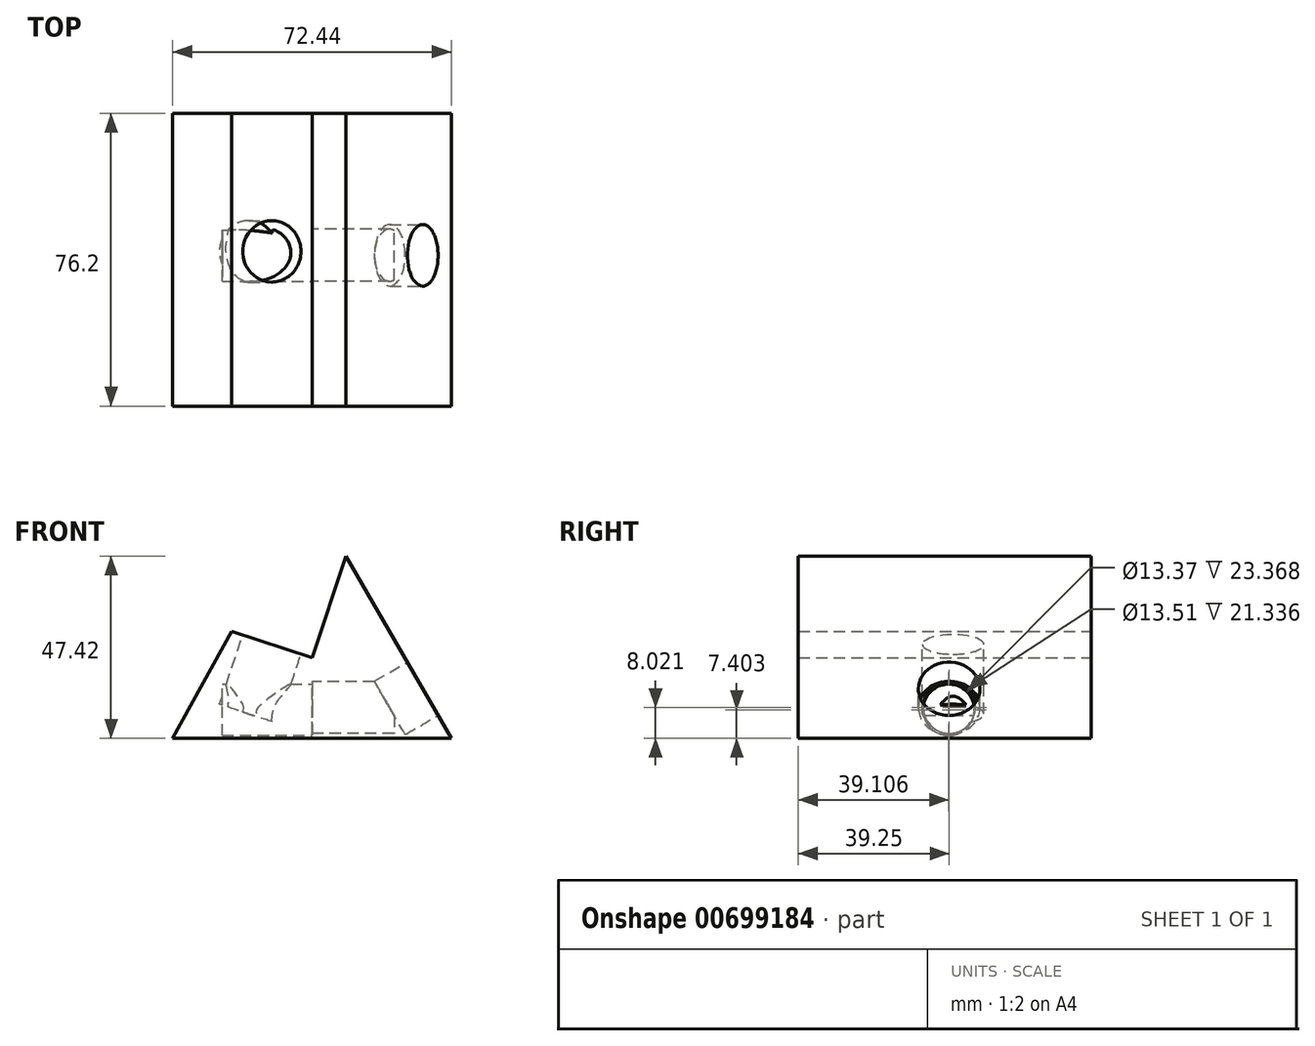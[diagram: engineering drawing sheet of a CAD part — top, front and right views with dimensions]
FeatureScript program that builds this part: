
annotation { "Feature Type Name" : "Feature", "Feature Type Description" : "" }
export const myFeature = defineFeature(function(context is Context, id is Id, definition is map)
    precondition{}
    {
        {
            var Q0;
            Q0=qCreatedBy(makeId("Front.planeOp"),FACE);
            var sketch = newSketch(context, id + "F0", { "sketchPlane" : qUnion([Q0])});
            skLineSegment(sketch, "E0.0", {"start": v(36.22, -20.9) * mm, "end": v(-36.22, -20.9) * mm});
            skLineSegment(sketch, "E0.1", {"start": v(-36.22, -20.9) * mm, "end": v(-20.9, 6.97) * mm});
            skLineSegment(sketch, "E0.2", {"start": v(8.84, 26.51) * mm, "end": v(36.22, -20.9) * mm});
            skPoint(sketch, "E0.0.midPoint", {"position": v(0, -20.9) * mm});
            skPoint(sketch, "E0.cCircle.center.orphan", {"position": v(0, 0) * mm});
            skLineSegment(sketch, "E1", {"start": v(-20.9, 6.97) * mm, "end": v(0, 0) * mm});
            skLineSegment(sketch, "E2", {"start": v(0, 0) * mm, "end": v(8.84, 26.51) * mm});
            skSolve(sketch);
        }
        {
            var Q0;
            Q0 = qSketchRegion(id + "F0", true);
            extrude(context, id + "F1", {"entities" : qUnion([Q0]), "depth" : 76.2 * mm, "offsetDistance" : 25.4 * mm});
        }
        {
            var Q0;
            Q0=makeQuery(id+"F1.opExtrude","SWEPT_FACE",FACE,{"disambiguationData":[OSD([sQuery(id+"F0.wireOp",EDGE,"E1")])]});
            var sketch = newSketch(context, id + "F2", { "sketchPlane" : qUnion([Q0])});
            skCircle(sketch, "E3", {"center": v(-11.03, -35.95) * mm, "radius": 7.99 * mm});
            skSolve(sketch);
        }
        {
            var Q0;
            Q0 = qSketchRegion(id + "F2", true);
            extrude(context, id + "F3", {"entities" : qUnion([Q0]), "operationType" : NewBodyOperationType.REMOVE, "oppositeDirection" : true, "depth" : 19.05 * mm, "offsetDistance" : 25.4 * mm});
        }
        {
            var Q0;
            Q0=makeQuery(id+"F1.opExtrude","SWEPT_FACE",FACE,{"disambiguationData":[OSD([sQuery(id+"F0.wireOp",EDGE,"E0.2")])]});
            var sketch = newSketch(context, id + "F4", { "sketchPlane" : qUnion([Q0])});
            skCircle(sketch, "E4", {"center": v(-36.98, -21.37) * mm, "radius": 7.99 * mm});
            skSolve(sketch);
        }
        {
            var Q0;
            Q0 = qSketchRegion(id + "F4", true);
            extrude(context, id + "F5", {"entities" : qUnion([Q0]), "operationType" : NewBodyOperationType.REMOVE, "oppositeDirection" : true, "depth" : 9.9 * mm, "offsetDistance" : 25.4 * mm});
        }
        {
            var Q0;
            Q0=qCreatedBy(makeId("Right.planeOp"),FACE);
            var sketch = newSketch(context, id + "F6", { "sketchPlane" : qUnion([Q0])});
            skCircle(sketch, "E5", {"center": v(-37.1, -13.5) * mm, "radius": 6.68 * mm});
            skSolve(sketch);
        }
        {
            var Q0;
            Q0 = qSketchRegion(id + "F6", true);
            extrude(context, id + "F7", {"entities" : qUnion([Q0]), "operationType" : NewBodyOperationType.REMOVE, "oppositeDirection" : true, "depth" : 23.37 * mm, "offsetDistance" : 25.4 * mm});
        }
        {
            var Q0;
            Q0=qCreatedBy(makeId("Right.planeOp"),FACE);
            var sketch = newSketch(context, id + "F8", { "sketchPlane" : qUnion([Q0])});
            skCircle(sketch, "E6", {"center": v(-36.95, -12.89) * mm, "radius": 6.76 * mm});
            skSolve(sketch);
        }
        {
            var Q0;
            Q0 = qSketchRegion(id + "F8", true);
            extrude(context, id + "F9", {"entities" : qUnion([Q0]), "operationType" : NewBodyOperationType.REMOVE, "depth" : 21.34 * mm, "offsetDistance" : 25.4 * mm});
        }
    });
